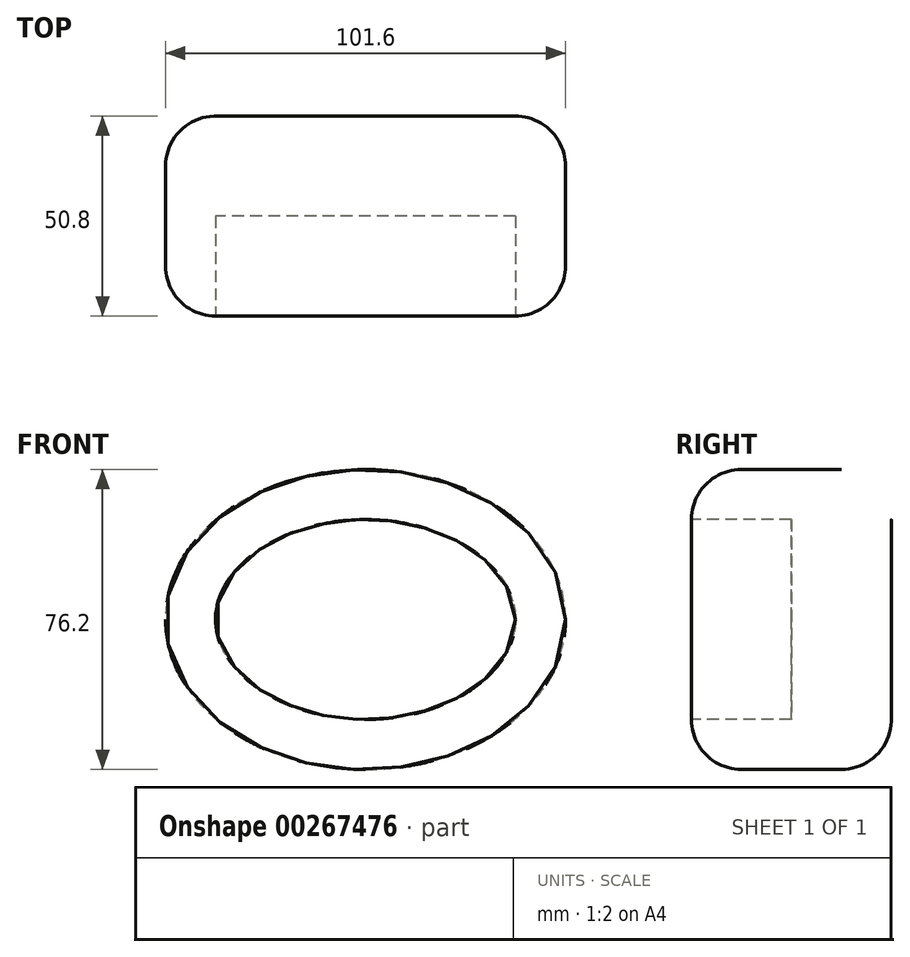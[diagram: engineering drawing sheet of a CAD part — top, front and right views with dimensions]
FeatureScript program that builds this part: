
annotation { "Feature Type Name" : "Feature", "Feature Type Description" : "" }
export const myFeature = defineFeature(function(context is Context, id is Id, definition is map)
    precondition{}
    {
        {
            var Q0;
            Q0=qCreatedBy(makeId("Front.planeOp"),FACE);
            var sketch = newSketch(context, id + "F0", { "sketchPlane" : qUnion([Q0])});
            skEllipse(sketch, "E0", {"center": v(0, 0) * mm, "majorRadius": 50.8 * mm, "minorRadius": 38.1 * mm, "majorAxis": v(1, 0)});
            skSolve(sketch);
        }
        {
            var Q0;
            Q0 = qSketchRegion(id + "F0", true);
            extrude(context, id + "F1", {"entities" : qUnion([Q0]), "depth" : 50.8 * mm});
        }
        {
            var Q0;
            Q0=makeQuery(id+"F1.opExtrude","SWEPT_FACE",FACE,{"disambiguationData":[OSD([sQuery(id+"F0.wireOp",EDGE,"E0")])]});
            fillet(context, id + "F2", {"entities" : qUnion([Q0]), "radius" : 12.7 * mm, "tangentPropagation" : true, "allowEdgeOverflow" : false});
        }
        {
            var Q0;
            Q0=makeQuery(id+"F1.opExtrude","CAP_FACE",FACE,{"disambiguationData":[OSD([sQuery(id+"F0.wireOp",EDGE,"E0")])],"isStart":false});
            extrude(context, id + "F3", {"entities" : qUnion([Q0]), "operationType" : NewBodyOperationType.REMOVE, "oppositeDirection" : true, "depth" : 25.4 * mm});
        }
    });
